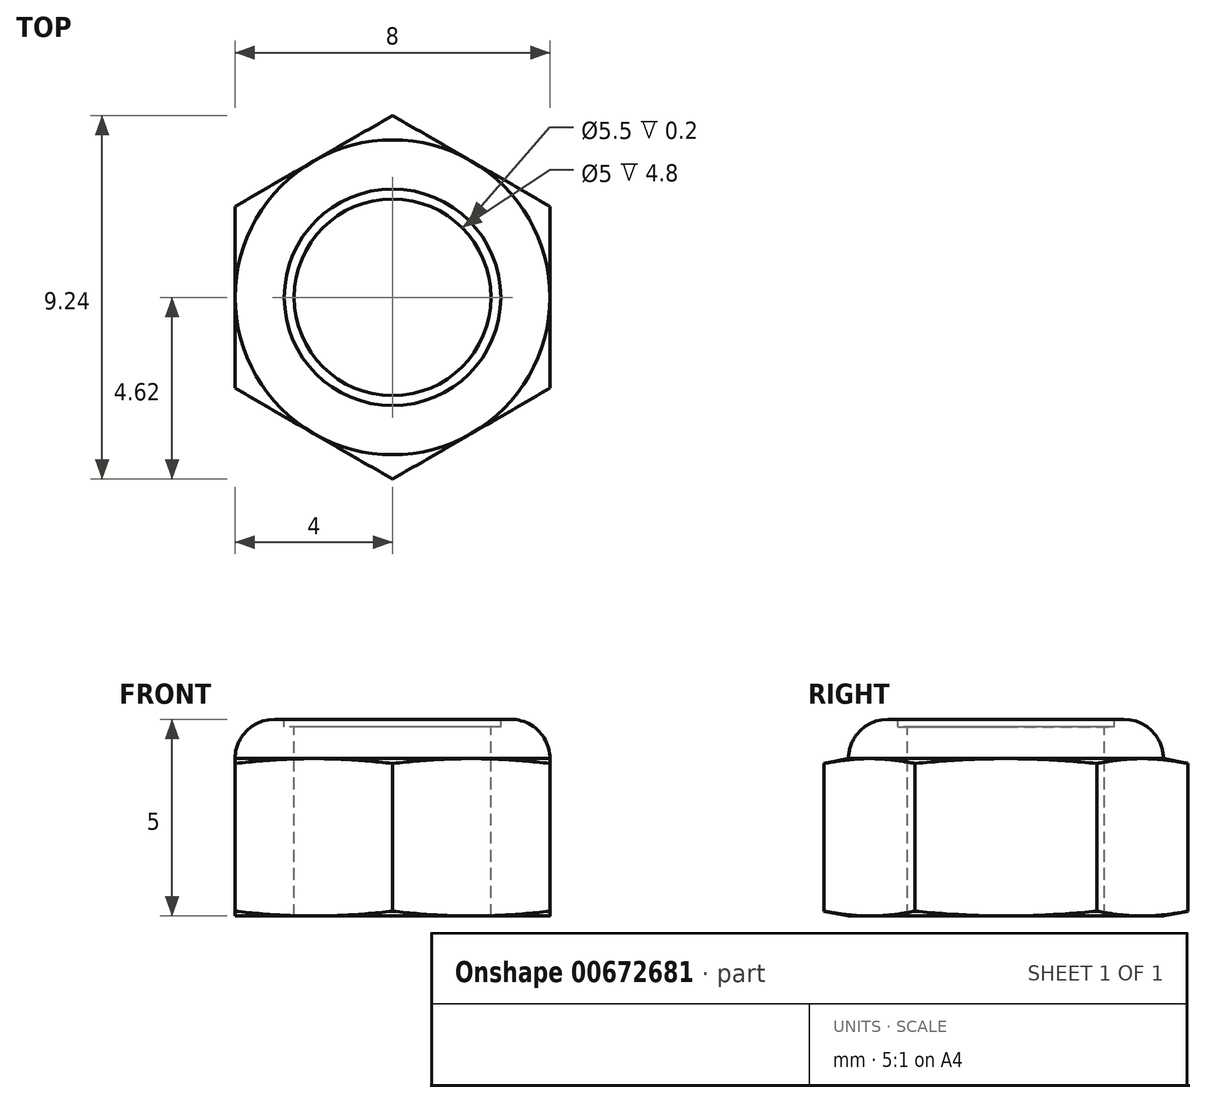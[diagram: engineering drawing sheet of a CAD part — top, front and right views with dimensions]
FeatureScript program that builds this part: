
annotation { "Feature Type Name" : "Feature", "Feature Type Description" : "" }
export const myFeature = defineFeature(function(context is Context, id is Id, definition is map)
    precondition{}
    {
        {
            var Q0;
            Q0=qCreatedBy(makeId("Top.planeOp"),FACE);
            var sketch = newSketch(context, id + "F0", { "sketchPlane" : qUnion([Q0])});
            skCircle(sketch, "E0", {"center": v(0, 0) * mm, "radius": 6 * mm});
            skSolve(sketch);
        }
        {
            var Q0;
            Q0=makeQuery(id+"F0.imprint","IMPRINT",FACE,{"disambiguationData":[TD([[makeQuery(id+"F0.imprint","IMPRINT",EDGE,{"derivedFrom":sQuery(id+"F0.wireOp",EDGE,"E0")}),1.0]])]});
            extrude(context, id + "F1", {"entities" : qUnion([Q0]), "depth" : 4 * mm, "offsetDistance" : 25 * mm});
        }
        {
            var Q0;
            Q0=makeQuery(id+"F1.opExtrude","CAP_EDGE",EDGE,{"disambiguationData":[OSD([sQuery(id+"F0.wireOp",EDGE,"E0")])],"isStart":false});
            var Q1;
            Q1=makeQuery(id+"F1.opExtrude","CAP_EDGE",EDGE,{"disambiguationData":[OSD([sQuery(id+"F0.wireOp",EDGE,"E0")])],"isStart":true});
            chamfer(context, id + "F2", {"entities" : qUnion([Q0, Q1]), "chamferType" : ChamferType.TWO_OFFSETS, "width1" : 2 * mm, "oppositeDirection" : false, "width2" : .4 * mm, "tangentPropagation" : true});
        }
        {
            var Q0;
            Q0=makeQuery(id+"F1.opExtrude","CAP_FACE",FACE,{"disambiguationData":[OSD([sQuery(id+"F0.wireOp",EDGE,"E0")])],"isStart":false});
            var sketch = newSketch(context, id + "F3", { "sketchPlane" : qUnion([Q0])});
            skCircle(sketch, "E1.cCircle", {"center": v(0, 0) * mm, "radius": 4 * mm, "construction": true});
            skLineSegment(sketch, "E1.0", {"start": v(4, 2.3) * mm, "end": v(4, -2.3) * mm});
            skLineSegment(sketch, "E1.1", {"start": v(4, -2.3) * mm, "end": v(0, -4.62) * mm});
            skLineSegment(sketch, "E1.2", {"start": v(0, -4.62) * mm, "end": v(-4, -2.3) * mm});
            skLineSegment(sketch, "E1.3", {"start": v(-4, -2.3) * mm, "end": v(-4, 2.3) * mm});
            skLineSegment(sketch, "E1.4", {"start": v(-4, 2.3) * mm, "end": v(0, 4.62) * mm});
            skLineSegment(sketch, "E1.5", {"start": v(0, 4.62) * mm, "end": v(4, 2.3) * mm});
            skPoint(sketch, "E1.0.midPoint", {"position": v(4, 0) * mm});
            skSolve(sketch);
        }
        {
            var Q0;
            {var subQ0=sQuery(id+"F3.wireOp",EDGE,"E1.3");var subQ1=sQuery(id+"F3.wireOp",EDGE,"E1.2");var subQ2=makeQuery(id+"F3.imprint","INTERSECT",VERTEX,{"derivedFrom":[subQ1,subQ0]});Q0=makeQuery(id+"F3.imprint","IMPRINT",FACE,{"disambiguationData":[TD([[makeQuery(id+"F3.imprint","IMPRINT",EDGE,{"disambiguationData":[TD([[subQ2,1.0]])],"derivedFrom":subQ1}),-1.0]])]});}
            var Q1;
            {var subQ0=sQuery(id+"F3.wireOp",EDGE,"E1.4");var subQ1=sQuery(id+"F3.wireOp",EDGE,"E1.3");var subQ2=makeQuery(id+"F3.imprint","INTERSECT",VERTEX,{"derivedFrom":[subQ1,subQ0]});Q1=makeQuery(id+"F3.imprint","IMPRINT",FACE,{"disambiguationData":[TD([[makeQuery(id+"F3.imprint","IMPRINT",EDGE,{"disambiguationData":[TD([[subQ2,1.0]])],"derivedFrom":subQ1}),-1.0]])]});}
            var Q2;
            {var subQ0=sQuery(id+"F3.wireOp",EDGE,"E1.5");var subQ1=sQuery(id+"F3.wireOp",EDGE,"E1.4");var subQ2=makeQuery(id+"F3.imprint","INTERSECT",VERTEX,{"derivedFrom":[subQ1,subQ0]});Q2=makeQuery(id+"F3.imprint","IMPRINT",FACE,{"disambiguationData":[TD([[makeQuery(id+"F3.imprint","IMPRINT",EDGE,{"disambiguationData":[TD([[subQ2,1.0]])],"derivedFrom":subQ1}),-1.0]])]});}
            var Q3;
            {var subQ0=sQuery(id+"F3.wireOp",EDGE,"E1.5");var subQ1=sQuery(id+"F3.wireOp",EDGE,"E1.0");var subQ2=makeQuery(id+"F3.imprint","INTERSECT",VERTEX,{"derivedFrom":[subQ1,subQ0]});Q3=makeQuery(id+"F3.imprint","IMPRINT",FACE,{"disambiguationData":[TD([[makeQuery(id+"F3.imprint","IMPRINT",EDGE,{"disambiguationData":[TD([[subQ2,-1.0]])],"derivedFrom":subQ1}),-1.0]])]});}
            var Q4;
            {var subQ0=sQuery(id+"F3.wireOp",EDGE,"E1.1");var subQ1=sQuery(id+"F3.wireOp",EDGE,"E1.0");var subQ2=makeQuery(id+"F3.imprint","INTERSECT",VERTEX,{"derivedFrom":[subQ1,subQ0]});Q4=makeQuery(id+"F3.imprint","IMPRINT",FACE,{"disambiguationData":[TD([[makeQuery(id+"F3.imprint","IMPRINT",EDGE,{"disambiguationData":[TD([[subQ2,1.0]])],"derivedFrom":subQ1}),-1.0]])]});}
            var Q5;
            {var subQ0=sQuery(id+"F3.wireOp",EDGE,"E1.2");var subQ1=sQuery(id+"F3.wireOp",EDGE,"E1.1");var subQ2=makeQuery(id+"F3.imprint","INTERSECT",VERTEX,{"derivedFrom":[subQ1,subQ0]});Q5=makeQuery(id+"F3.imprint","IMPRINT",FACE,{"disambiguationData":[TD([[makeQuery(id+"F3.imprint","IMPRINT",EDGE,{"disambiguationData":[TD([[subQ2,1.0]])],"derivedFrom":subQ1}),-1.0]])]});}
            var Q6;
            {var subQ0=sQuery(id+"F0.wireOp",EDGE,"E0");var subQ1=makeQuery(id+"F2.opChamfer","BLEND_EDGE",EDGE,{"blendedFrom":[makeQuery(id+"F1.opExtrude","CAP_EDGE",EDGE,{"disambiguationData":[OSD([subQ0])],"isStart":false}),makeQuery(id+"F1.opExtrude","CAP_FACE",FACE,{"disambiguationData":[OSD([subQ0])],"isStart":false})],"blendedInto":[makeQuery(id+"F1.opExtrude","CAP_FACE",FACE,{"disambiguationData":[OSD([subQ0])],"isStart":false})]});var subQ5=makeQuery(id+"F3.imprint","INTERSECT",VERTEX,{"derivedFrom":[subQ1,sQuery(id+"F3.wireOp",EDGE,"E1.0")]});Q6=makeQuery(id+"F3.imprint","IMPRINT",FACE,{"disambiguationData":[TD([[makeQuery(id+"F3.imprint","IMPRINT",EDGE,{"disambiguationData":[TD([[subQ5,1.0]])],"derivedFrom":subQ1}),1.0]])]});}
            extrude(context, id + "F4", {"entities" : qUnion([Q0, Q1, Q2, Q3, Q4, Q5, Q6]), "operationType" : NewBodyOperationType.INTERSECT, "oppositeDirection" : true, "depth" : 25 * mm, "offsetDistance" : 25 * mm});
        }
        {
            var Q0;
            Q0=makeQuery(id+"F1.opExtrude","CAP_FACE",FACE,{"disambiguationData":[OSD([sQuery(id+"F0.wireOp",EDGE,"E0")])],"isStart":false});
            var sketch = newSketch(context, id + "F5", { "sketchPlane" : qUnion([Q0])});
            skCircle(sketch, "E2", {"center": v(0, 0) * mm, "radius": 4 * mm});
            skSolve(sketch);
        }
        {
            var Q0;
            {var subQ0=sQuery(id+"F5.wireOp",EDGE,"E2");var subQ5=makeQuery(id+"F5.imprint","IMPRINT",VERTEX,{"disambiguationData":[OD(0.0)],"derivedFrom":subQ0});Q0=makeQuery(id+"F5.imprint","IMPRINT",FACE,{"disambiguationData":[TD([[makeQuery(id+"F5.imprint","IMPRINT",EDGE,{"disambiguationData":[TD([[subQ5,-1.0]])],"derivedFrom":subQ0}),1.0]])]});}
            extrude(context, id + "F6", {"entities" : qUnion([Q0]), "operationType" : NewBodyOperationType.ADD, "depth" : 1 * mm, "offsetDistance" : 25 * mm});
        }
        {
            var Q0;
            Q0=makeQuery(id+"F6.opExtrude","CAP_EDGE",EDGE,{"disambiguationData":[OSD([sQuery(id+"F5.wireOp",EDGE,"E2")])],"isStart":false});
            fillet(context, id + "F7", {"entities" : qUnion([Q0]), "radius" : 1 * mm, "tangentPropagation" : true, "allowEdgeOverflow" : false});
        }
        {
            var Q0;
            Q0=makeQuery(id+"F6.opExtrude","CAP_FACE",FACE,{"disambiguationData":[OSD([sQuery(id+"F5.wireOp",EDGE,"E2")])],"isStart":false});
            var sketch = newSketch(context, id + "F8", { "sketchPlane" : qUnion([Q0])});
            skCircle(sketch, "E3", {"center": v(0, 0) * mm, "radius": 2.75 * mm});
            skSolve(sketch);
        }
        {
            var Q0;
            Q0=makeQuery(id+"F8.imprint","IMPRINT",FACE,{"disambiguationData":[TD([[makeQuery(id+"F8.imprint","IMPRINT",EDGE,{"derivedFrom":sQuery(id+"F8.wireOp",EDGE,"E3")}),1.0]])]});
            extrude(context, id + "F9", {"entities" : qUnion([Q0]), "operationType" : NewBodyOperationType.REMOVE, "oppositeDirection" : true, "depth" : .2 * mm, "offsetDistance" : 25 * mm});
        }
        {
            var Q0;
            Q0=makeQuery(id+"F9.boolean.opBoolean","COPY",FACE,{"derivedFrom":makeQuery(id+"F9.opExtrude","CAP_FACE",FACE,{"disambiguationData":[OSD([sQuery(id+"F8.wireOp",EDGE,"E3")])],"isStart":false})});
            var sketch = newSketch(context, id + "F10", { "sketchPlane" : qUnion([Q0])});
            skCircle(sketch, "E4", {"center": v(0, 0) * mm, "radius": 2.5 * mm});
            skSolve(sketch);
        }
        {
            var Q0;
            Q0=makeQuery(id+"F10.imprint","IMPRINT",FACE,{"disambiguationData":[TD([[makeQuery(id+"F10.imprint","IMPRINT",EDGE,{"derivedFrom":sQuery(id+"F10.wireOp",EDGE,"E4")}),1.0]])]});
            extrude(context, id + "F11", {"entities" : qUnion([Q0]), "operationType" : NewBodyOperationType.REMOVE, "oppositeDirection" : true, "depth" : 25 * mm, "offsetDistance" : 25 * mm});
        }
    });
